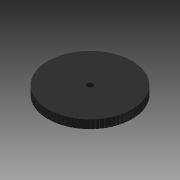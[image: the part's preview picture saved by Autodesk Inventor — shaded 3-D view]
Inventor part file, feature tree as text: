
AUTODESK INVENTOR PART (.ipt)
format: ipt  version: 2014 (Build 180170000, 170)  size: 395,264 bytes
history: native  units: in
note: dims shown in document units (in); Inventor stores cm internally (conversion verified against a paired STEP export)
features: other x3, sketch x3
ambient origin geometry x8: Origin, YZ Plane, XZ Plane, XY Plane, X Axis, Y Axis, Z Axis, Center Point
bodies: Solid1 (feature_tree)
feature tree (6):
  other  "wheel 1.ipt"
  other  "Solid1::wheel 1.ipt"
  other  "TaggingFeature1"
  sketch  "Sketch1"  dims[d0=0.3937in]
  sketch  "Sketch2"  dims[d1=0.3937in d2=0.0in d3=0.2756in d4=0.3937in d5=0.0in d7=0.3937in d8=0.0in d9=31.4961in d10=360.0deg]
  sketch  "Sketch3"
